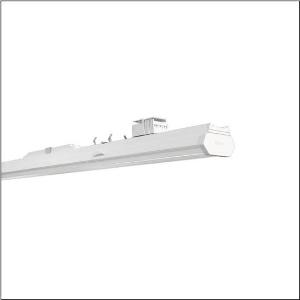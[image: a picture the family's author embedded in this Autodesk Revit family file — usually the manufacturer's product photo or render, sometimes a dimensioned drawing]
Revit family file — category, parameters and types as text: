
# Revit family: licross_r__21_protected_ho_52td12dn4e5m_4ef7
name_source: partatom
category: Lighting Fixtures
units: mm (PartAtom-declared; Revit-internal decimal feet)

## family parameters
Cut with Voids When Loaded = No
Host = Face
Light Source = No
Part Type = Normal
Room Calculation Point = No
Round Connector Dimension = Use Diameter
Shared = No

## types (1)
- --- (1 x LED, 14690 lm, 84.9 W, 4000K)
    Apparent Load = 85 VA
    CIE Flux Codes = 70 91 97 98 100
    Color Rendering = 80
    Color Temperature = 4000K
    Default Elevation = 1800 mm
    Description = Licross® 21 Protected HO, luminaire insert, of sheet steel, galvanised, coil coated, white, length: 1.500mm, width: 90mm, height: 103mm, LED rated luminous flux: 14.690lm, light colour: 840, control gear: DALI 2, with plug, 5-pole, with phase selection, mains connection: 220..240V, AC, 50/60Hz, rated input power: 85W, halogen-free wiring, primary light control with lens, of plastic, primary optical cover: cover, of PMMA, light emission: direct distribution, primary light characteristic: symmetric, protection rating (complete): IP54, insulation class (complete): insulation class I (protective earthing), certification: CE, ENEC, VDE, UKCA, protection symbol: D if used in an environment with non-conductive dust loads with corresponding accessories, impact resistance: IK06, permissible ambient temperature for indoor applications: -25..+35°C, corresponds to IFS (International Featured Standards) requirements for safety and quality in the food industry, reducing of maximum allowable ambient temperature of 5°C with ceiling mounting, LABS conformity tested according to VDMA 24364:2018-05, packaging unit: 1 piece
    Height = 92 mm
    Lamp = 1 x LED
    Lamp Light Flux = 14690 lm
    Lamp Power = 84.9 W
    Lamp count = 1
    Length = 1500 mm
    Luminous efficacy = 173 lm/W
    Manufacturer = Siteco
    ModVariant = No
    Model = 52TD12DN4E5M
    Mounting Place = Ceiling
    Mounting Type = Pendant
    Number of Poles = 1
    OnlyDefault = Yes
    Power Factor = 1
    Product Name = Licross® 21 Protected HO
    Product group = luminaire insert
    ProductGroupID = 901
    Protection Class = Protection class I
    Protection Degree = IP 54
    RLX_Detail_Level = 1
    RLX_Emergency_Light_Flux = 0 lm
    RLX_Emergency_Type = 0
    RLX_Emergency_Type_DB = No
    RlxData = <blob elided: 24449 chars, md5=7dd7aa34>
    Socket = socket
    Standby Power = 0 W
    System Light Flux = 14690 lm
    System Power = 85 W
    Type Comments = factory setting: luminous flux: 100 % | dim-lin: 254 | 484 mA
    Type Image = l_1256148.jpg
    URL = http://relux.com
    VarID = @adj_078703
    Voltage = 0 V
    Weight = 0.00 kg
    Width = 88 mm

## geometry (parser evidence)
native form markers: Blend x4, Sweep x8
no freeform markers — native parametric forms only
